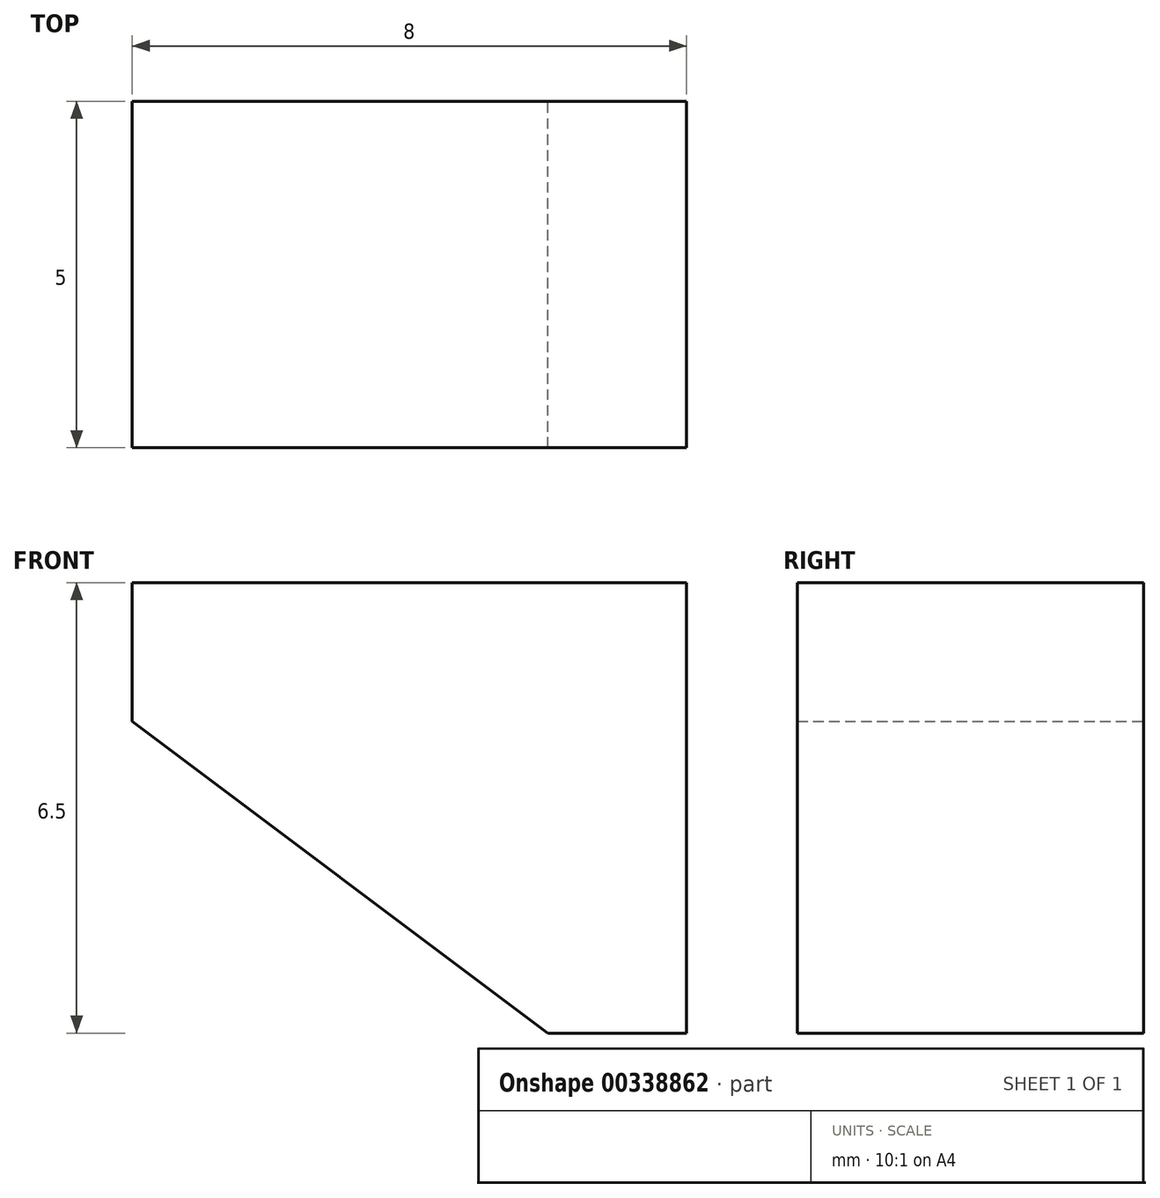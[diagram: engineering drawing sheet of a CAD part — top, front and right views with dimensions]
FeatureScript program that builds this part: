
annotation { "Feature Type Name" : "Feature", "Feature Type Description" : "" }
export const myFeature = defineFeature(function(context is Context, id is Id, definition is map)
    precondition{}
    {
        {
            var Q0;
            Q0=qCreatedBy(makeId("Front.planeOp"),FACE);
            var sketch = newSketch(context, id + "F0", { "sketchPlane" : qUnion([Q0])});
            skLineSegment(sketch, "E0", {"start": v(0, 0) * mm, "end": v(0, 2) * mm});
            skLineSegment(sketch, "E1", {"start": v(0, 2) * mm, "end": v(8, 2) * mm});
            skLineSegment(sketch, "E2", {"start": v(8, 2) * mm, "end": v(8, -4.5) * mm});
            skLineSegment(sketch, "E3", {"start": v(8, -4.5) * mm, "end": v(6, -4.5) * mm});
            skLineSegment(sketch, "E4", {"start": v(6, -4.5) * mm, "end": v(0, 0) * mm});
            skSolve(sketch);
        }
        {
            var Q0;
            Q0 = qSketchRegion(id + "F0", true);
            extrude(context, id + "F1", {"entities" : qUnion([Q0]), "depth" : 5 * mm});
        }
    });
